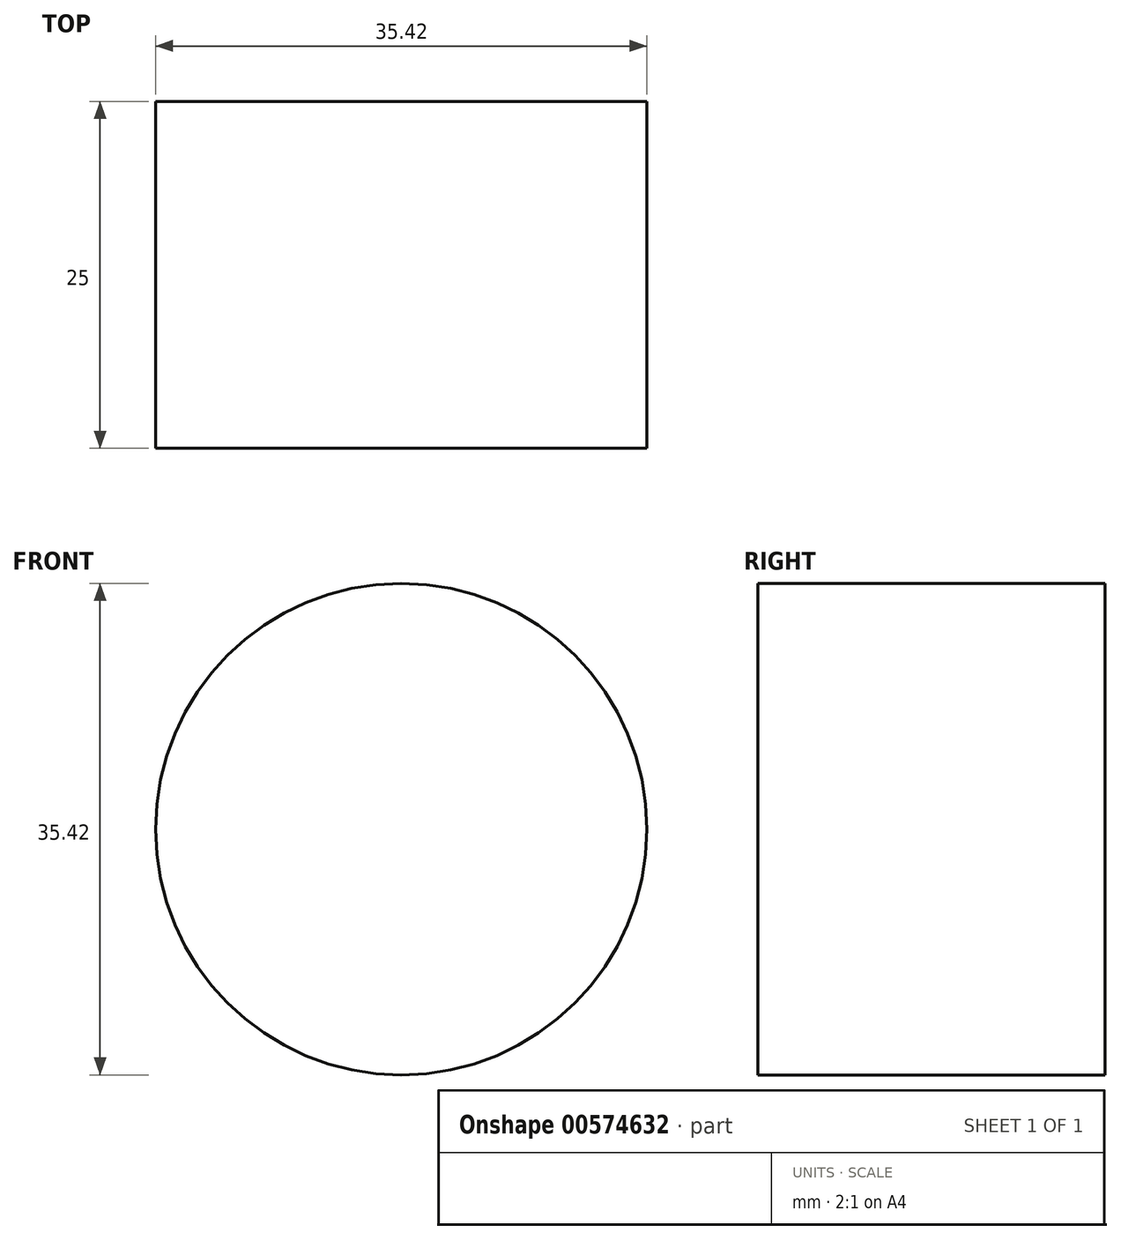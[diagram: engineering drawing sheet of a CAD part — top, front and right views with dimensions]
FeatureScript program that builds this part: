
annotation { "Feature Type Name" : "Feature", "Feature Type Description" : "" }
export const myFeature = defineFeature(function(context is Context, id is Id, definition is map)
    precondition{}
    {
        {
            var Q0;
            Q0=qCreatedBy(makeId("Front.planeOp"),FACE);
            var sketch = newSketch(context, id + "F0", { "sketchPlane" : qUnion([Q0])});
            skCircle(sketch, "E0", {"center": v(-54.15, 48.33) * mm, "radius": 17.7 * mm});
            skSolve(sketch);
        }
        {
            var Q0;
            Q0 = qSketchRegion(id + "F0", true);
            extrude(context, id + "F1", {"entities" : qUnion([Q0]), "depth" : 25 * mm, "offsetDistance" : 25 * mm});
        }
    });
